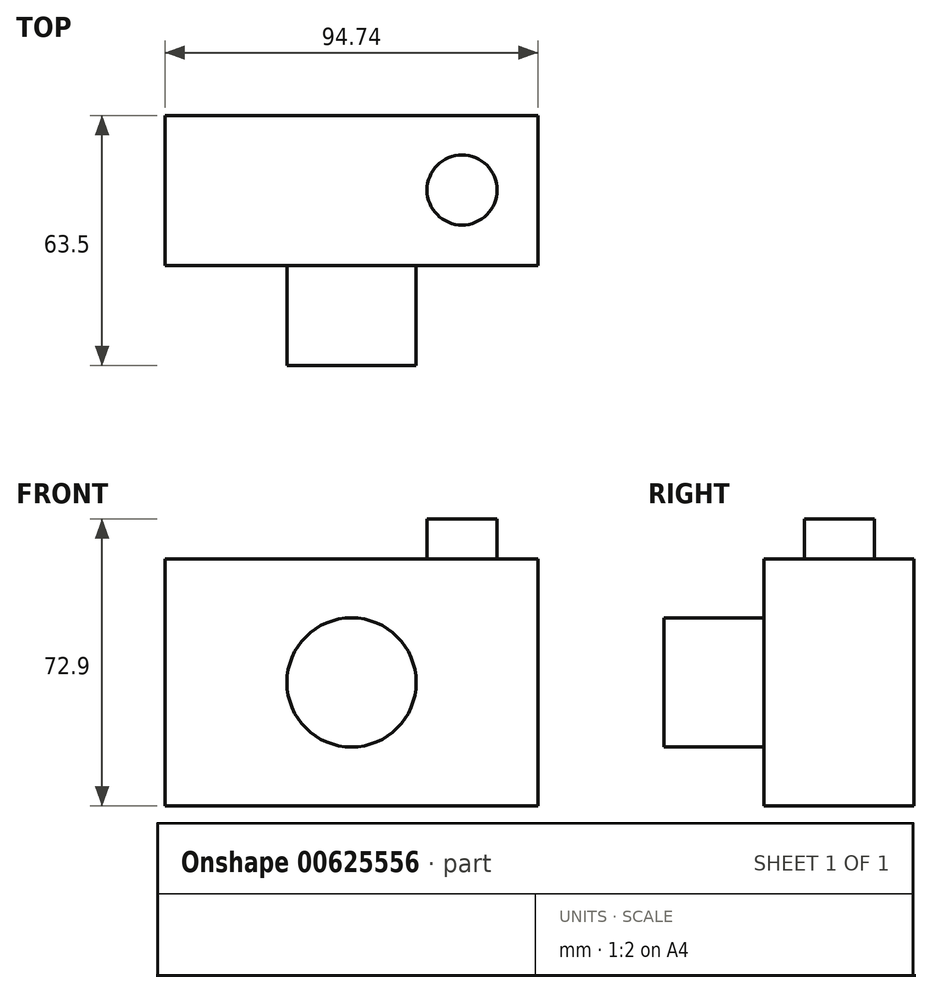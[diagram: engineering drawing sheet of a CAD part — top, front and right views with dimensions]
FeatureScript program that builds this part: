
annotation { "Feature Type Name" : "Feature", "Feature Type Description" : "" }
export const myFeature = defineFeature(function(context is Context, id is Id, definition is map)
    precondition{}
    {
        {
            var Q0;
            Q0=qCreatedBy(makeId("Front.planeOp"),FACE);
            var sketch = newSketch(context, id + "F0", { "sketchPlane" : qUnion([Q0])});
            skLineSegment(sketch, "E0.bottom", {"start": v(47.37, 31.37) * mm, "end": v(-47.37, 31.37) * mm});
            skLineSegment(sketch, "E0.top", {"start": v(47.37, -31.37) * mm, "end": v(-47.37, -31.37) * mm});
            skLineSegment(sketch, "E0.left", {"start": v(47.37, 31.37) * mm, "end": v(47.37, -31.37) * mm});
            skLineSegment(sketch, "E0.right", {"start": v(-47.37, 31.37) * mm, "end": v(-47.37, -31.37) * mm});
            skPoint(sketch, "E0.middle", {"position": v(0, 0) * mm});
            skSolve(sketch);
        }
        {
            var Q0;
            Q0=makeQuery(id+"F0.imprint","IMPRINT",FACE,{"disambiguationData":[TD([[makeQuery(id+"F0.imprint","IMPRINT",EDGE,{"derivedFrom":sQuery(id+"F0.wireOp",EDGE,"E0.bottom")}),1.0]])]});
            extrude(context, id + "F1", {"entities" : qUnion([Q0]), "depth" : 38.1 * mm, "offsetDistance" : 25.4 * mm});
        }
        {
            var Q0;
            Q0=makeQuery(id+"F1.opExtrude","CAP_FACE",FACE,{"disambiguationData":[OSD([sQuery(id+"F0.wireOp",EDGE,"E0.bottom"),sQuery(id+"F0.wireOp",EDGE,"E0.top"),sQuery(id+"F0.wireOp",EDGE,"E0.left"),sQuery(id+"F0.wireOp",EDGE,"E0.right")])],"isStart":false});
            var sketch = newSketch(context, id + "F2", { "sketchPlane" : qUnion([Q0])});
            skCircle(sketch, "E1", {"center": v(0, 0) * mm, "radius": 16.41 * mm});
            skSolve(sketch);
        }
        {
            var Q0;
            Q0=makeQuery(id+"F2.imprint","IMPRINT",FACE,{"disambiguationData":[TD([[makeQuery(id+"F2.imprint","IMPRINT",EDGE,{"derivedFrom":sQuery(id+"F2.wireOp",EDGE,"E1")}),1.0]])]});
            extrude(context, id + "F3", {"entities" : qUnion([Q0]), "operationType" : NewBodyOperationType.ADD, "depth" : 25.4 * mm, "offsetDistance" : 25.4 * mm, "hasSecondDirection" : true, "secondDirectionOppositeDirection" : true, "secondDirectionDepth" : 12.7 * mm});
        }
        {
            var Q0;
            Q0=makeQuery(id+"F1.opExtrude","SWEPT_FACE",FACE,{"disambiguationData":[OSD([sQuery(id+"F0.wireOp",EDGE,"E0.bottom")])]});
            var sketch = newSketch(context, id + "F4", { "sketchPlane" : qUnion([Q0])});
            skCircle(sketch, "E2", {"center": v(28.07, -18.92) * mm, "radius": 8.9 * mm});
            skSolve(sketch);
        }
        {
            var Q0;
            Q0=makeQuery(id+"F4.imprint","IMPRINT",FACE,{"disambiguationData":[TD([[makeQuery(id+"F4.imprint","IMPRINT",EDGE,{"derivedFrom":sQuery(id+"F4.wireOp",EDGE,"E2")}),1.0]])]});
            extrude(context, id + "F5", {"entities" : qUnion([Q0]), "operationType" : NewBodyOperationType.ADD, "depth" : 10.16 * mm, "offsetDistance" : 25.4 * mm});
        }
    });
